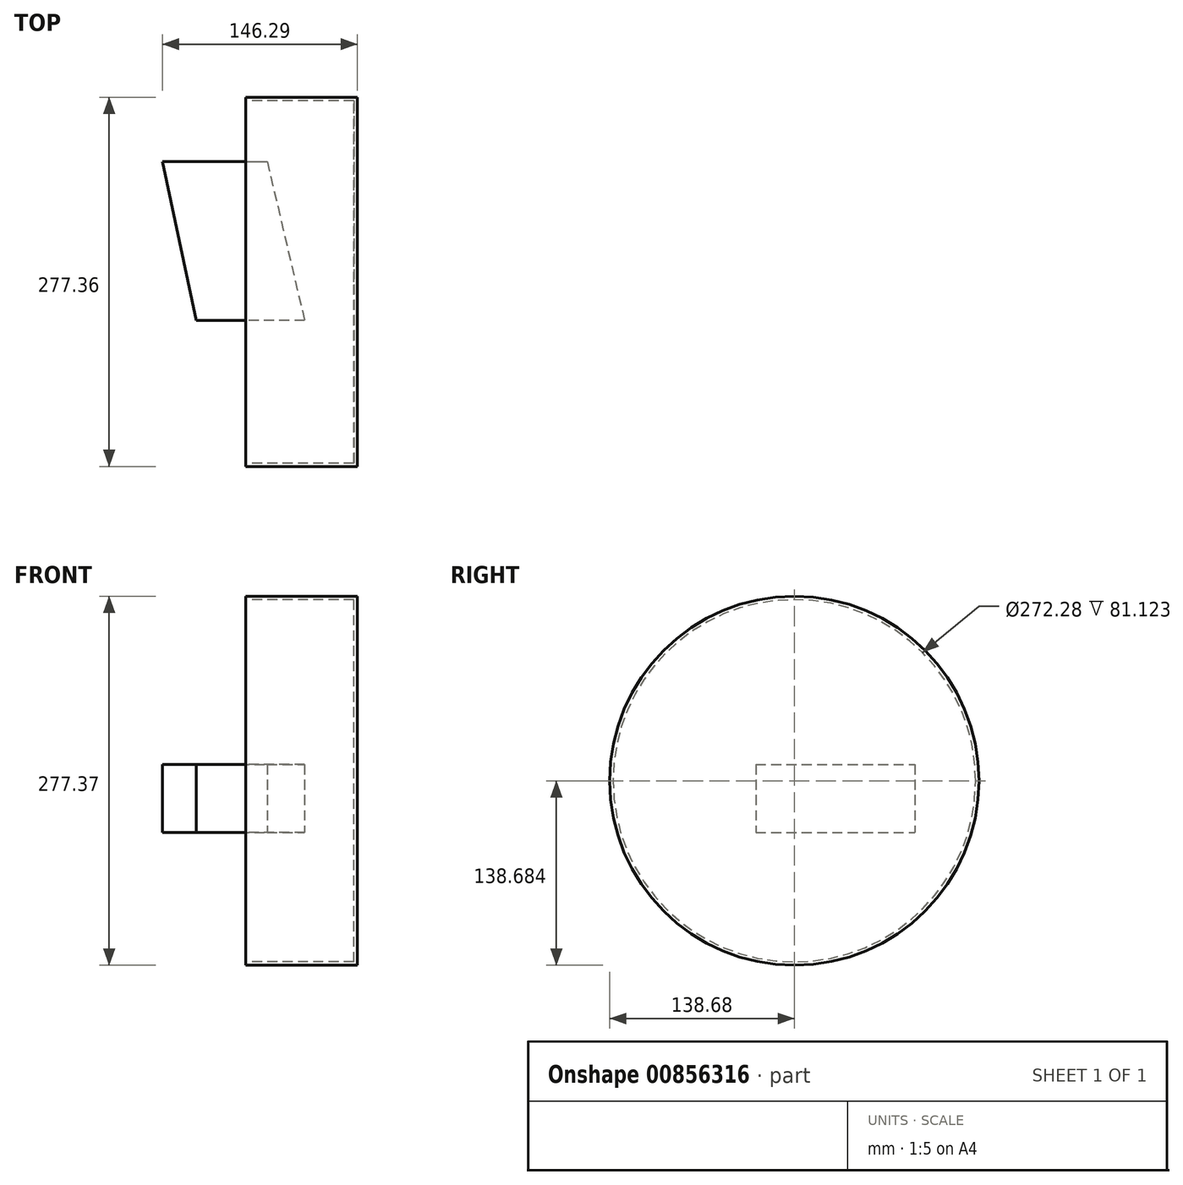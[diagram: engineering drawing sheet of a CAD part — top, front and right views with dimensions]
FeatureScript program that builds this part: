
annotation { "Feature Type Name" : "Feature", "Feature Type Description" : "" }
export const myFeature = defineFeature(function(context is Context, id is Id, definition is map)
    precondition{}
    {
        {
            var Q0;
            Q0=qCreatedBy(makeId("Top.planeOp"),FACE);
            var sketch = newSketch(context, id + "F0", { "sketchPlane" : qUnion([Q0])});
            skLineSegment(sketch, "E0", {"start": v(-62.63, 41.32) * mm, "end": v(16, 41.32) * mm});
            skLineSegment(sketch, "E1", {"start": v(16, 41.32) * mm, "end": v(44.07, -78.19) * mm});
            skLineSegment(sketch, "E2", {"start": v(44.07, -78.19) * mm, "end": v(-37.37, -78.19) * mm});
            skLineSegment(sketch, "E3", {"start": v(-37.37, -78.19) * mm, "end": v(-62.63, 41.32) * mm});
            skSolve(sketch);
        }
        {
            var Q0;
            Q0=makeQuery(id+"F0.imprint","IMPRINT",FACE,{"disambiguationData":[TD([[makeQuery(id+"F0.imprint","IMPRINT",EDGE,{"derivedFrom":sQuery(id+"F0.wireOp",EDGE,"E0")}),-1.0]])]});
            var sketch = newSketch(context, id + "F1", { "sketchPlane" : qUnion([Q0])});
            skSolve(sketch);
        }
        {
            var Q0;
            Q0=makeQuery(id+"F1.imprint","IMPRINT",FACE,{"disambiguationData":[TD([[makeQuery(id+"F1.imprint","IMPRINT",EDGE,{"derivedFrom":makeQuery(id+"F0.imprint","IMPRINT",EDGE,{"derivedFrom":sQuery(id+"F0.wireOp",EDGE,"E0")})}),-1.0]])]});
            var Q1;
            Q1=makeQuery(id+"F0.imprint","IMPRINT",FACE,{"disambiguationData":[TD([[makeQuery(id+"F0.imprint","IMPRINT",EDGE,{"derivedFrom":sQuery(id+"F0.wireOp",EDGE,"E0")}),-1.0]])]});
            extrude(context, id + "F2", {"entities" : qUnion([Q0, Q1]), "depth" : 51.27 * mm, "offsetDistance" : 25.4 * mm});
        }
        {
            var Q0;
            Q0=qCreatedBy(makeId("Right.planeOp"),FACE);
            var sketch = newSketch(context, id + "F3", { "sketchPlane" : qUnion([Q0])});
            skCircle(sketch, "E4", {"center": v(-49.23, 39) * mm, "radius": 138.68 * mm});
            skSolve(sketch);
        }
        {
            var Q0;
            Q0=makeQuery(id+"F3.imprint","IMPRINT",FACE,{"disambiguationData":[TD([[makeQuery(id+"F3.imprint","IMPRINT",EDGE,{"derivedFrom":sQuery(id+"F3.wireOp",EDGE,"E4")}),1.0]])]});
            extrude(context, id + "F4", {"entities" : qUnion([Q0]), "depth" : 83.66 * mm, "offsetDistance" : 25.4 * mm});
        }
        {
            var Q0;
            Q0=makeQuery(id+"F4.opExtrude","CAP_FACE",FACE,{"disambiguationData":[OSD([sQuery(id+"F3.wireOp",EDGE,"E4")])],"isStart":true});
            shell(context, id + "F5", {"entities" : qUnion([Q0]), "thickness" : 2.54 * mm});
        }
    });
